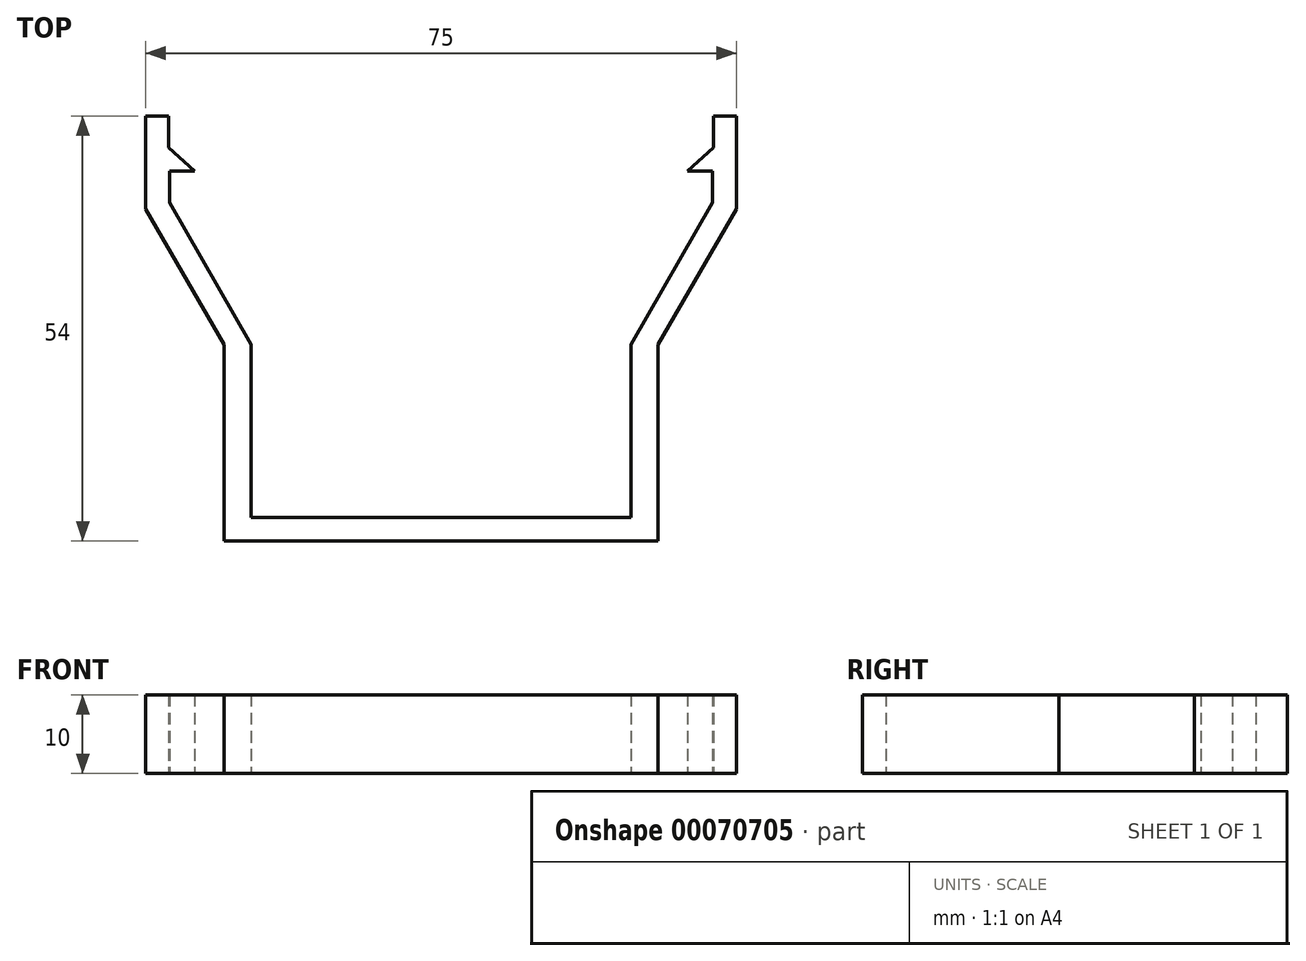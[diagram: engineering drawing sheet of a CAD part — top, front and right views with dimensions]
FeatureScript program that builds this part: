
annotation { "Feature Type Name" : "Feature", "Feature Type Description" : "" }
export const myFeature = defineFeature(function(context is Context, id is Id, definition is map)
    precondition{}
    {
        {
            var Q0;
            Q0=qCreatedBy(makeId("Top.planeOp"),FACE);
            var sketch = newSketch(context, id + "F0", { "sketchPlane" : qUnion([Q0])});
            skLineSegment(sketch, "E0", {"start": v(27.58, 0) * mm, "end": v(37.5, 17.2) * mm});
            skLineSegment(sketch, "E1", {"start": v(37.5, 17.2) * mm, "end": v(37.5, 25) * mm});
            skLineSegment(sketch, "E2", {"start": v(25.85, 3) * mm, "end": v(34.5, 18) * mm});
            skLineSegment(sketch, "E3", {"start": v(34.5, 18) * mm, "end": v(34.5, 22) * mm});
            skLineSegment(sketch, "E4", {"start": v(37.5, 25) * mm, "end": v(34.64, 25) * mm});
            skLineSegment(sketch, "E5", {"start": v(34.5, 22) * mm, "end": v(31.3, 22) * mm});
            skLineSegment(sketch, "E6", {"start": v(31.3, 22) * mm, "end": v(34.64, 25) * mm});
            skLineSegment(sketch, "E7.0.MirrorCS", {"start": v(-34.5, 22) * mm, "end": v(-31.3, 22) * mm});
            skLineSegment(sketch, "E7.1.MirrorCS", {"start": v(-31.3, 22) * mm, "end": v(-34.64, 25) * mm});
            skLineSegment(sketch, "E7.2.MirrorCS", {"start": v(-37.5, 25) * mm, "end": v(-34.64, 25) * mm});
            skLineSegment(sketch, "E7.4.MirrorCS", {"start": v(-25.85, 3) * mm, "end": v(-34.5, 18) * mm});
            skLineSegment(sketch, "E7.6.MirrorCS", {"start": v(-37.5, 17.2) * mm, "end": v(-37.5, 25) * mm});
            skLineSegment(sketch, "E7.7.MirrorCS", {"start": v(-34.5, 18) * mm, "end": v(-34.5, 22) * mm});
            skLineSegment(sketch, "E7.8.MirrorCS", {"start": v(-27.58, 0) * mm, "end": v(-37.5, 17.2) * mm});
            skLineSegment(sketch, "E8", {"start": v(-37.5, 25) * mm, "end": v(-37.5, 29) * mm});
            skLineSegment(sketch, "E9", {"start": v(-37.5, 29) * mm, "end": v(-34.64, 29) * mm});
            skLineSegment(sketch, "E10", {"start": v(-34.64, 29) * mm, "end": v(-34.64, 25) * mm});
            skLineSegment(sketch, "E11.MirrorCS", {"start": v(37.5, 29) * mm, "end": v(34.64, 29) * mm});
            skLineSegment(sketch, "E12.MirrorCS", {"start": v(37.5, 25) * mm, "end": v(37.5, 29) * mm});
            skLineSegment(sketch, "E13.MirrorCS", {"start": v(34.64, 29) * mm, "end": v(34.64, 25) * mm});
            skLineSegment(sketch, "E14", {"start": v(-25.85, 3) * mm, "end": v(-24.12, 0) * mm});
            skLineSegment(sketch, "E15.MirrorCS", {"start": v(25.85, 3) * mm, "end": v(24.12, 0) * mm});
            skLineSegment(sketch, "E16", {"start": v(-24.12, 0) * mm, "end": v(-24.12, -22) * mm});
            skLineSegment(sketch, "E17.MirrorCS", {"start": v(24.12, 0) * mm, "end": v(24.12, -22) * mm});
            skLineSegment(sketch, "E18", {"start": v(-24.12, -22) * mm, "end": v(24.12, -22) * mm});
            skLineSegment(sketch, "E19", {"start": v(-27.58, 0) * mm, "end": v(-27.58, -25) * mm});
            skLineSegment(sketch, "E20.MirrorCS", {"start": v(27.58, 0) * mm, "end": v(27.58, -25) * mm});
            skLineSegment(sketch, "E21", {"start": v(-27.58, -25) * mm, "end": v(27.58, -25) * mm});
            skSolve(sketch);
        }
        {
            var Q0;
            Q0=makeQuery(id+"F0.imprint","IMPRINT",FACE,{"disambiguationData":[TD([[makeQuery(id+"F0.imprint","IMPRINT",EDGE,{"derivedFrom":sQuery(id+"F0.wireOp",EDGE,"E7.2.MirrorCS")}),1.0]])]});
            var Q1;
            Q1=makeQuery(id+"F0.imprint","IMPRINT",FACE,{"disambiguationData":[TD([[makeQuery(id+"F0.imprint","IMPRINT",EDGE,{"derivedFrom":sQuery(id+"F0.wireOp",EDGE,"E4")}),-1.0]])]});
            var Q2;
            Q2=makeQuery(id+"F0.imprint","IMPRINT",FACE,{"disambiguationData":[TD([[makeQuery(id+"F0.imprint","IMPRINT",EDGE,{"derivedFrom":sQuery(id+"F0.wireOp",EDGE,"E0")}),1.0]])]});
            extrude(context, id + "F1", {"entities" : qUnion([Q0, Q1, Q2]), "depth" : 10 * mm});
        }
    });
